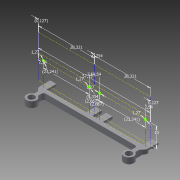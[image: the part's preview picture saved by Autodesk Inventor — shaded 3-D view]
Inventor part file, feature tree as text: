
AUTODESK INVENTOR PART (.ipt)
format: ipt  version: 2015 (Build 190159000, 159)  size: 265,216 bytes
history: native  units: in
note: dims shown in document units (in); Inventor stores cm internally (conversion verified against a paired STEP export)
features: sketch x7, extrude x6, pattern_linear x6, projected_geometry x2
ambient origin geometry x8: Origin, YZ Plane, XZ Plane, XY Plane, X Axis, Y Axis, Z Axis, Center Point
bodies: Solid1 (feature_tree)
feature tree (21):
  extrude  "Extrusion1"  Depth=1.95in
  extrude  "Extrusion2"  Depth=0.1969in
  extrude  "Extrusion3"  Depth=0.1181in TaperAngle=0.0deg
  pattern_linear  "Rectangular Pattern1"  Spacing1=0.0866in  [1 undecoded]
  extrude  "Extrusion4"  Depth=0.0394in
  pattern_linear  "Rectangular Pattern2"  Spacing1=0.0787in  [1 undecoded]
  pattern_linear  "Rectangular Pattern3"  Spacing1=0.1181in  [1 undecoded]
  extrude  "Extrusion5"  Depth=0.045in
  extrude  "Extrusion6"  Depth=0.1969in TaperAngle=0.0deg
  pattern_linear  "Rectangular Pattern4"  Spacing1=0.9094in  [1 undecoded]
  pattern_linear  "Rectangular Pattern5"  Spacing1=0.0394in  [1 undecoded]
  pattern_linear  "Rectangular Pattern6"  Spacing1=0.0394in  [1 undecoded]
  sketch  "Sketch8"  dims[d17=0.0787in d18=0.0866in d19=0.0394in d20=0.0787in d21=0.1181in d22=0.0in d23=0.045in d24=0.1969in d25=0.0in d26=0.9094in d27=0.0394in d28=0.0394in d29=0.025in d30=0.025in d31=0.0591in d32=0.7874in d34=0.915in d35=0.0841in d36=0.0in d37=0.7874in d39=0.21in d40=0.7874in d42=1.125in d43=0.0841in d44=0.0in d46=0.0787in d47=0.0in d48=0.7874in d50=0.915in d51=0.7874in d53=1.125in d54=0.7874in d56=2.04in d57=2.25in d58=0.3937in d59=1.115in d60=0.005in d61=1.115in d62=0.01in d63=0.005in d64=0.05in d65=0.1in d66=0.05in d67=0.1in d68=0.05in d69=0.05in d70=0.1in d71=0.1in d72=0.915in d73=0.21in d74=0.915in d75=0.105in d76=0.105in]
  sketch  "Sketch1"  dims[d0=0.125in d2=1.95in]
  sketch  "Sketch2"  dims[d3=0.125in d4=0.1969in]
  sketch  "Sketch3"  dims[d11=0.1969in d12=0.1181in d13=0.0in]
  sketch  "Sketch4"  dims[d14=0.1969in]
  sketch  "Sketch6"  dims[d15=0.0866in]
  sketch  "Sketch7"  dims[d16=0.0787in]
  projected_geometry  "Projected Loop1"
  projected_geometry  "Projected Loop2"
note: 6 required parameter values undecoded (feature->parameter linkage not recoverable at this tier; creation-order binding heuristic only, values carry confidence <= 0.55)
